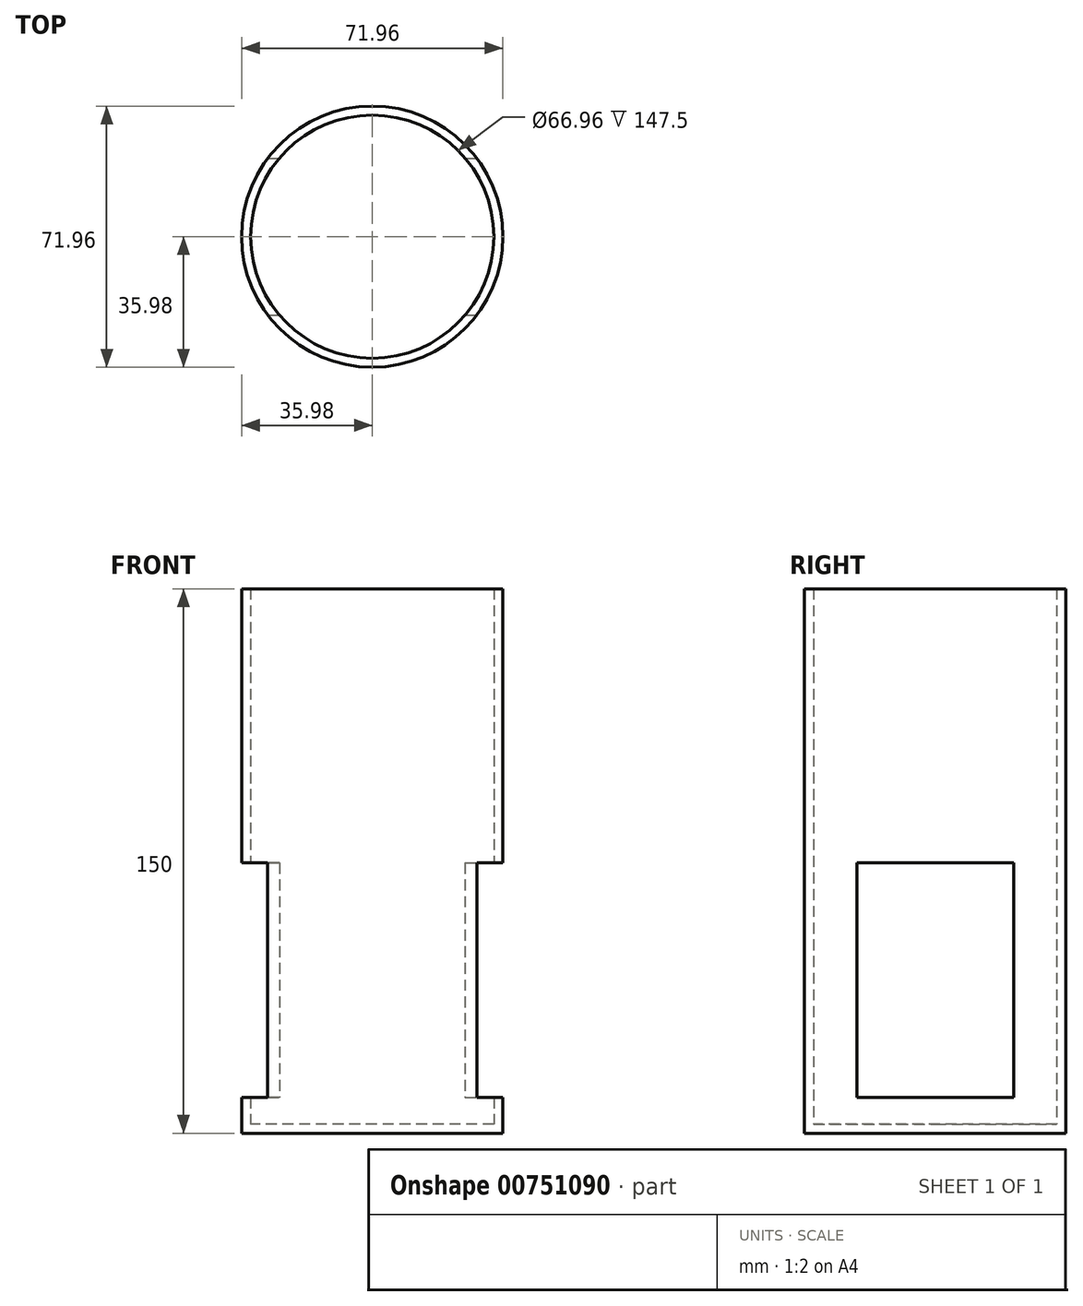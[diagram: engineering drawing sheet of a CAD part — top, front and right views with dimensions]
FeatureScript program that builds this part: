
annotation { "Feature Type Name" : "Feature", "Feature Type Description" : "" }
export const myFeature = defineFeature(function(context is Context, id is Id, definition is map)
    precondition{}
    {
        {
            var Q0;
            Q0=qCreatedBy(makeId("Top.planeOp"),FACE);
            var sketch = newSketch(context, id + "F0", { "sketchPlane" : qUnion([Q0])});
            skCircle(sketch, "E0", {"center": v(0, 0) * mm, "radius": 35.98 * mm});
            skLineSegment(sketch, "E1", {"start": v(35.98, 0) * mm, "end": v(35.98, 74.33) * mm});
            skLineSegment(sketch, "E2", {"start": v(35.98, 0) * mm, "end": v(35.98, -74.87) * mm});
            skSolve(sketch);
        }
        {
            var Q0;
            Q0=makeQuery(id+"F0.imprint","IMPRINT",FACE,{"disambiguationData":[TD([[makeQuery(id+"F0.imprint","IMPRINT",EDGE,{"derivedFrom":sQuery(id+"F0.wireOp",EDGE,"E0")}),1.0]])]});
            extrude(context, id + "F1", {"entities" : qUnion([Q0]), "depth" : 150 * mm, "offsetDistance" : 25 * mm});
        }
        {
            var Q0;
            Q0=makeQuery(id+"F1.opExtrude","CAP_FACE",FACE,{"disambiguationData":[OSD([sQuery(id+"F0.wireOp",EDGE,"E0")])],"isStart":false});
            shell(context, id + "F2", {"entities" : qUnion([Q0]), "thickness" : 2.5 * mm});
        }
        {
            var Q0;
            Q0=sQuery(id+"F0.wireOp",EDGE,"E2");
            var Q1;
            Q1=sQuery(id+"F0.wireOp",EDGE,"E1");
            extrude(context, id + "F3", {"bodyType" : ToolBodyType.SURFACE, "surfaceEntities" : qUnion([Q0, Q1]), "depth" : 150 * mm, "offsetDistance" : 25 * mm});
        }
        {
            var Q0;
            Q0=makeQuery(id+"F3.opExtrude","SWEPT_FACE",FACE,{"disambiguationData":[OSD([sQuery(id+"F0.wireOp",EDGE,"E1"),sQuery(id+"F0.wireOp",EDGE,"E2")])]});
            var sketch = newSketch(context, id + "F4", { "sketchPlane" : qUnion([Q0])});
            skLineSegment(sketch, "E3", {"start": v(0, 0) * mm, "end": v(0, 74.48) * mm});
            skLineSegment(sketch, "E4", {"start": v(0, 74.48) * mm, "end": v(21.61, 74.48) * mm});
            skLineSegment(sketch, "E5", {"start": v(21.61, 74.48) * mm, "end": v(21.61, 9.86) * mm});
            skLineSegment(sketch, "E6", {"start": v(21.61, 9.86) * mm, "end": v(0, 9.86) * mm});
            skPoint(sketch, "E7.end.orphan", {"position": v(-16.15, 74.48) * mm});
            skLineSegment(sketch, "E8.MirrorCS", {"start": v(0, 74.48) * mm, "end": v(-21.61, 74.48) * mm});
            skLineSegment(sketch, "E9.MirrorCS", {"start": v(-21.61, 74.48) * mm, "end": v(-21.61, 9.86) * mm});
            skLineSegment(sketch, "E10.MirrorCS", {"start": v(-21.61, 9.86) * mm, "end": v(0, 9.86) * mm});
            skSolve(sketch);
        }
        {
            var Q0;
            {var subQ0=sQuery(id+"F4.wireOp",EDGE,"E4");Q0=makeQuery(id+"F4.imprint","IMPRINT",FACE,{"disambiguationData":[TD([[makeQuery(id+"F4.imprint","IMPRINT",EDGE,{"derivedFrom":subQ0}),-1.0]])]});}
            var Q1;
            {var subQ0=sQuery(id+"F4.wireOp",EDGE,"E8.MirrorCS");Q1=makeQuery(id+"F4.imprint","IMPRINT",FACE,{"disambiguationData":[TD([[makeQuery(id+"F4.imprint","IMPRINT",EDGE,{"derivedFrom":subQ0}),1.0]])]});}
            extrude(context, id + "F5", {"entities" : qUnion([Q0, Q1]), "operationType" : NewBodyOperationType.REMOVE, "depth" : 150 * mm, "offsetDistance" : 25 * mm});
        }
    });
